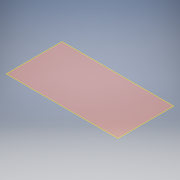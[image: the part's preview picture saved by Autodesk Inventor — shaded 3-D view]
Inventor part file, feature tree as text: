
AUTODESK INVENTOR PART (.ipt)
format: ipt  version: 2018 (Build 220112000, 112)  size: 89,088 bytes
history: native  units: mm
features: sketch x1, other x1, surface_op x1
ambient origin geometry x8: Origin, YZ Plane, XZ Plane, XY Plane, X Axis, Y Axis, Z Axis, Center Point
bodies: Body1 (feature_tree)
feature tree (3):
  sketch  "Sketch1"  dims[d0=100.0mm d1=50.0mm]
  other  "Srf1"
  surface_op  "Boundary Patch1"
